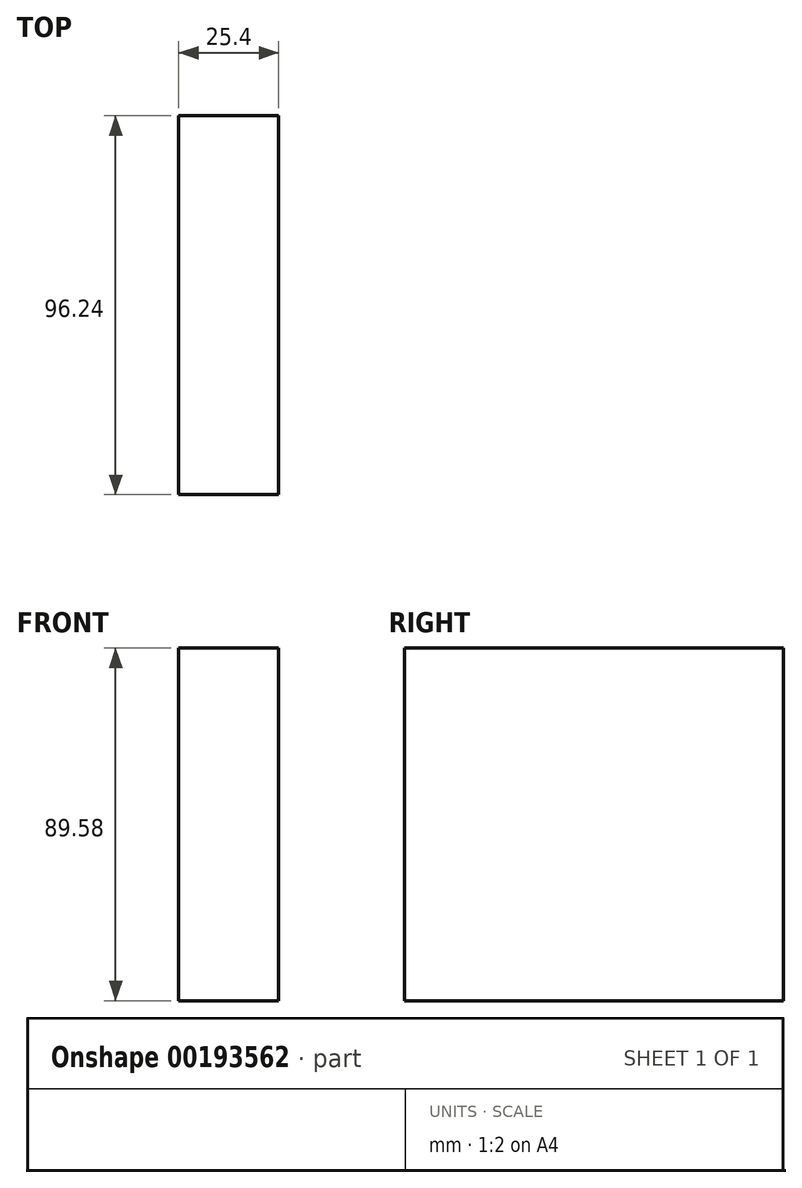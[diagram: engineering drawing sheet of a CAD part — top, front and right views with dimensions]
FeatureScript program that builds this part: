
annotation { "Feature Type Name" : "Feature", "Feature Type Description" : "" }
export const myFeature = defineFeature(function(context is Context, id is Id, definition is map)
    precondition{}
    {
        {
            var Q0;
            Q0=qCreatedBy(makeId("Right.planeOp"),FACE);
            var sketch = newSketch(context, id + "F0", { "sketchPlane" : qUnion([Q0])});
            skLineSegment(sketch, "E0.bottom", {"start": v(-48.12, -44.8) * mm, "end": v(48.12, -44.8) * mm});
            skLineSegment(sketch, "E0.top", {"start": v(-48.12, 44.8) * mm, "end": v(48.12, 44.8) * mm});
            skLineSegment(sketch, "E0.left", {"start": v(-48.12, -44.8) * mm, "end": v(-48.12, 44.8) * mm});
            skLineSegment(sketch, "E0.right", {"start": v(48.12, -44.8) * mm, "end": v(48.12, 44.8) * mm});
            skPoint(sketch, "E0.middle", {"position": v(0, 0) * mm});
            skSolve(sketch);
        }
        {
            var Q0;
            Q0=makeQuery(id+"F0.imprint","IMPRINT",FACE,{"disambiguationData":[TD([[makeQuery(id+"F0.imprint","IMPRINT",EDGE,{"derivedFrom":sQuery(id+"F0.wireOp",EDGE,"E0.bottom")}),1.0]])]});
            extrude(context, id + "F1", {"entities" : qUnion([Q0]), "depth" : 25.4 * mm});
        }
        {
            var Q0;
            Q0=makeQuery(id+"F1.opExtrude","CAP_FACE",FACE,{"disambiguationData":[OSD([sQuery(id+"F0.wireOp",EDGE,"E0.bottom"),sQuery(id+"F0.wireOp",EDGE,"E0.top"),sQuery(id+"F0.wireOp",EDGE,"E0.left"),sQuery(id+"F0.wireOp",EDGE,"E0.right")])],"isStart":true});
            var sketch = newSketch(context, id + "F2", { "sketchPlane" : qUnion([Q0])});
            skCircle(sketch, "E1", {"center": v(0, 0) * mm, "radius": 22.53 * mm});
            skSolve(sketch);
        }
        {
            var Q0;
            Q0=sQuery(id+"F2.wireOp",EDGE,"E1");
            extrude(context, id + "F3", {"bodyType" : ToolBodyType.SURFACE, "surfaceEntities" : qUnion([Q0]), "depth" : 25.4 * mm});
        }
    });
